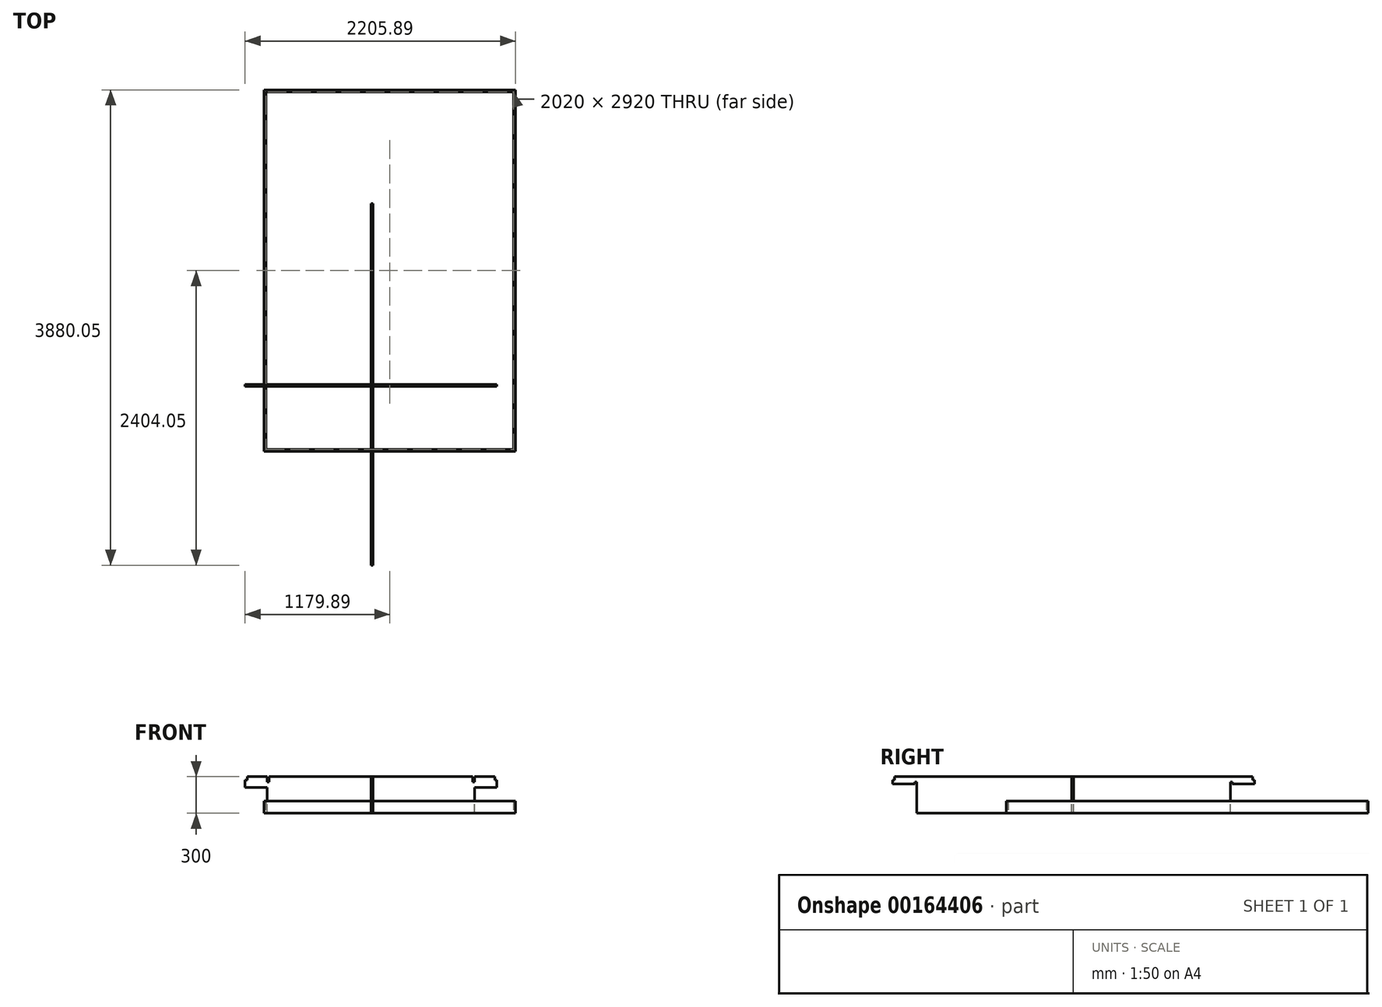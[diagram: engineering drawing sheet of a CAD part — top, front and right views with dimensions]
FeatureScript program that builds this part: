
annotation { "Feature Type Name" : "Feature", "Feature Type Description" : "" }
export const myFeature = defineFeature(function(context is Context, id is Id, definition is map)
    precondition{}
    {
        {
            var Q0;
            Q0=qCreatedBy(makeId("Front.planeOp"),FACE);
            var sketch = newSketch(context, id + "F0", { "sketchPlane" : qUnion([Q0])});
            skLineSegment(sketch, "E0.bottom", {"start": v(-846, 0) * mm, "end": v(846, 0) * mm});
            skLineSegment(sketch, "E0.left", {"start": v(-846, 0) * mm, "end": v(-846, 210) * mm});
            skLineSegment(sketch, "E0.right", {"start": v(846, 0) * mm, "end": v(846, 210) * mm});
            skLineSegment(sketch, "E1", {"start": v(-1010, 270) * mm, "end": v(-1026, 270) * mm});
            skLineSegment(sketch, "E2", {"start": v(-1026, 270) * mm, "end": v(-1026, 210) * mm});
            skLineSegment(sketch, "E3", {"start": v(-1026, 210) * mm, "end": v(-846, 210) * mm});
            skLineSegment(sketch, "E4", {"start": v(0, 0) * mm, "end": v(0, 270) * mm, "construction": true});
            skLineSegment(sketch, "E5.MirrorCS", {"start": v(1010, 270) * mm, "end": v(1026, 270) * mm});
            skLineSegment(sketch, "E6.MirrorCS", {"start": v(1026, 270) * mm, "end": v(1026, 210) * mm});
            skLineSegment(sketch, "E7.MirrorCS", {"start": v(1026, 210) * mm, "end": v(846, 210) * mm});
            skLineSegment(sketch, "E8", {"start": v(-1010, 270) * mm, "end": v(-1010, 300) * mm});
            skLineSegment(sketch, "E9.MirrorCS", {"start": v(1010, 270) * mm, "end": v(1010, 300) * mm});
            skLineSegment(sketch, "E10", {"start": v(-1010, 300) * mm, "end": v(-846, 300) * mm});
            skLineSegment(sketch, "E11", {"start": v(-846, 300) * mm, "end": v(-846, 255) * mm});
            skLineSegment(sketch, "E12", {"start": v(-846, 255) * mm, "end": v(-830, 255) * mm});
            skLineSegment(sketch, "E13", {"start": v(-830, 255) * mm, "end": v(-830, 300) * mm});
            skLineSegment(sketch, "E14.MirrorCS", {"start": v(830, 255) * mm, "end": v(830, 300) * mm});
            skLineSegment(sketch, "E15.MirrorCS", {"start": v(846, 255) * mm, "end": v(830, 255) * mm});
            skLineSegment(sketch, "E16.MirrorCS", {"start": v(846, 300) * mm, "end": v(846, 255) * mm});
            skLineSegment(sketch, "E17.trimOffspring", {"start": v(-830, 300) * mm, "end": v(830, 300) * mm});
            skLineSegment(sketch, "E18.trimOffspring", {"start": v(846, 300) * mm, "end": v(1010, 300) * mm});
            skSolve(sketch);
        }
        {
            var Q0;
            Q0 = qSketchRegion(id + "F0", true);
            extrude(context, id + "F1", {"entities" : qUnion([Q0]), "depth" : 16 * mm});
        }
        {
            var Q0;
            Q0=qCreatedBy(makeId("Right.planeOp"),FACE);
            var sketch = newSketch(context, id + "F2", { "sketchPlane" : qUnion([Q0])});
            skLineSegment(sketch, "E19", {"start": v(-1280, 0) * mm, "end": v(1280, 0) * mm});
            skLineSegment(sketch, "E20", {"start": v(-1280, 0) * mm, "end": v(-1280, 255) * mm});
            skLineSegment(sketch, "E21", {"start": v(-1280, 255) * mm, "end": v(-1296, 255) * mm});
            skLineSegment(sketch, "E22", {"start": v(-1296, 255) * mm, "end": v(-1296, 240) * mm});
            skLineSegment(sketch, "E23", {"start": v(-1296, 240) * mm, "end": v(-1476, 240) * mm});
            skLineSegment(sketch, "E24", {"start": v(-1476, 240) * mm, "end": v(-1476, 270) * mm});
            skLineSegment(sketch, "E25", {"start": v(-1476, 270) * mm, "end": v(-1460, 270) * mm});
            skLineSegment(sketch, "E26", {"start": v(-1460, 270) * mm, "end": v(-1460, 300) * mm});
            skLineSegment(sketch, "E27", {"start": v(0, 0) * mm, "end": v(0, 173.18) * mm, "construction": true});
            skLineSegment(sketch, "E28.MirrorCS", {"start": v(1280, 255) * mm, "end": v(1296, 255) * mm});
            skLineSegment(sketch, "E29.MirrorCS", {"start": v(1296, 255) * mm, "end": v(1296, 240) * mm});
            skLineSegment(sketch, "E30.MirrorCS", {"start": v(1296, 240) * mm, "end": v(1476, 240) * mm});
            skLineSegment(sketch, "E31.MirrorCS", {"start": v(1476, 240) * mm, "end": v(1476, 270) * mm});
            skLineSegment(sketch, "E32.MirrorCS", {"start": v(1476, 270) * mm, "end": v(1460, 270) * mm});
            skLineSegment(sketch, "E33.MirrorCS", {"start": v(1460, 270) * mm, "end": v(1460, 300) * mm});
            skLineSegment(sketch, "E34.MirrorCS", {"start": v(1280, 0) * mm, "end": v(1280, 255) * mm});
            skLineSegment(sketch, "E35", {"start": v(-1460, 300) * mm, "end": v(1460, 300) * mm});
            skSolve(sketch);
        }
        {
            var Q0;
            Q0 = qSketchRegion(id + "F2", true);
            extrude(context, id + "F3", {"entities" : qUnion([Q0]), "depth" : 16 * mm});
        }
        {
            var Q0;
            Q0=qCreatedBy(makeId("Top.planeOp"),FACE);
            var sketch = newSketch(context, id + "F4", { "sketchPlane" : qUnion([Q0])});
            skLineSegment(sketch, "E36.bottom", {"start": v(-872.1, -547.95) * mm, "end": v(1179.9, -547.95) * mm});
            skLineSegment(sketch, "E36.top", {"start": v(-872.1, 2404.05) * mm, "end": v(1179.9, 2404.05) * mm});
            skLineSegment(sketch, "E36.left", {"start": v(-872.1, -547.95) * mm, "end": v(-872.1, 2404.05) * mm});
            skLineSegment(sketch, "E36.right", {"start": v(1179.9, -547.95) * mm, "end": v(1179.9, 2404.05) * mm});
            skLineSegment(sketch, "E37.0", {"start": v(1163.9, -531.95) * mm, "end": v(1163.9, 2388.05) * mm});
            skLineSegment(sketch, "E37.1", {"start": v(-856.1, -531.95) * mm, "end": v(1163.9, -531.95) * mm});
            skLineSegment(sketch, "E37.2", {"start": v(-856.1, -531.95) * mm, "end": v(-856.1, 2388.05) * mm});
            skLineSegment(sketch, "E37.3", {"start": v(-856.1, 2388.05) * mm, "end": v(1163.9, 2388.05) * mm});
            skSolve(sketch);
        }
        {
            var Q0;
            Q0 = qSketchRegion(id + "F4", true);
            extrude(context, id + "F5", {"entities" : qUnion([Q0]), "depth" : 100 * mm});
        }
    });
